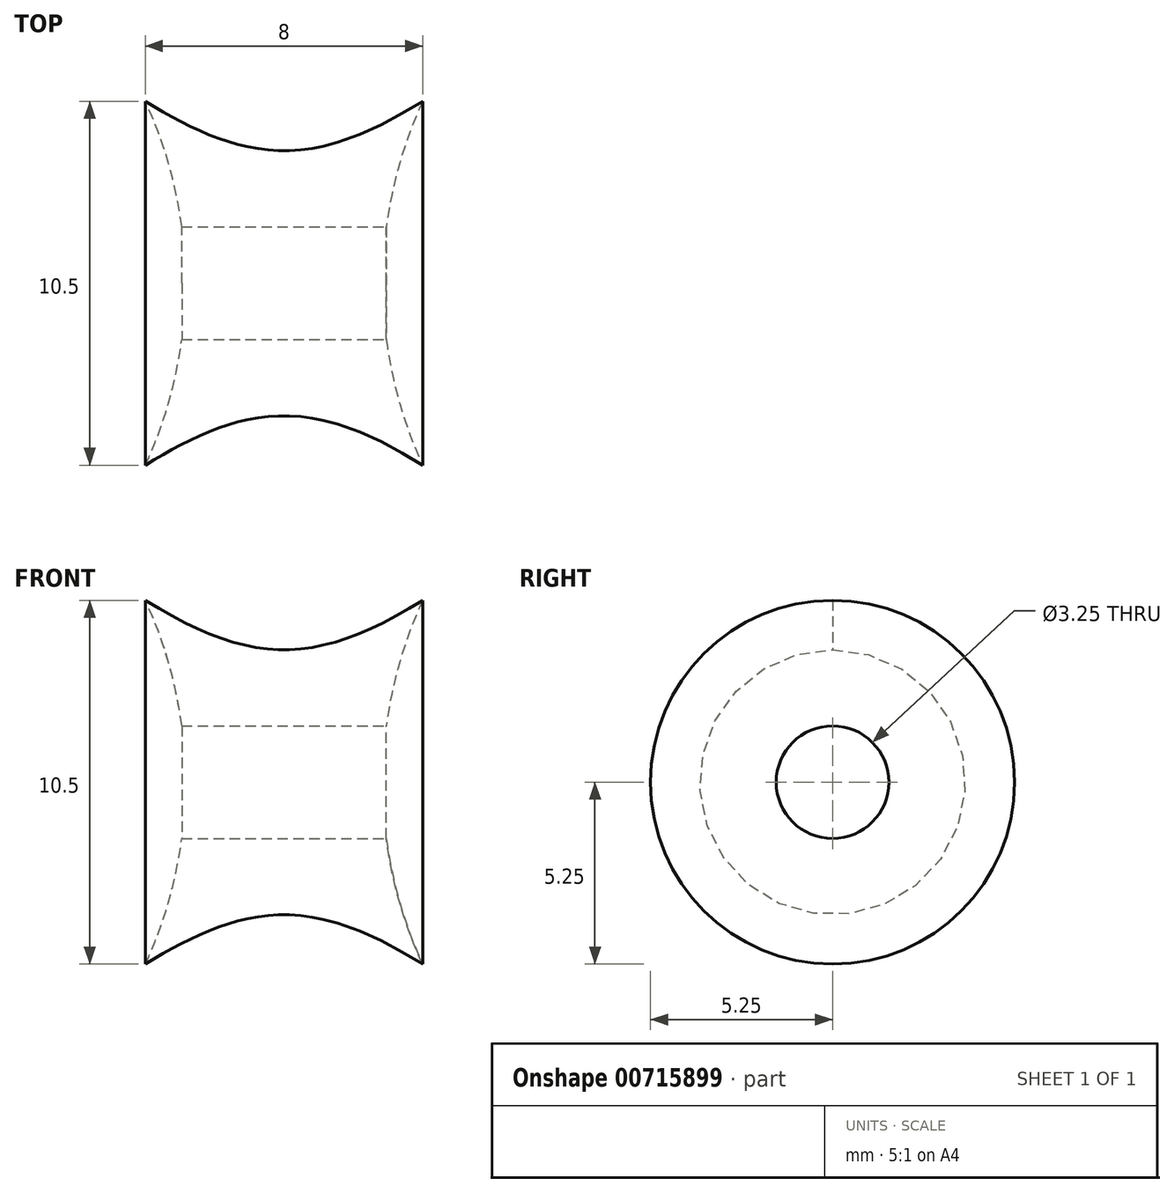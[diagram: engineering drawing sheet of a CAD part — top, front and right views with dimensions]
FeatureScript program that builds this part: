
annotation { "Feature Type Name" : "Feature", "Feature Type Description" : "" }
export const myFeature = defineFeature(function(context is Context, id is Id, definition is map)
    precondition{}
    {
        {
            var Q0;
            Q0=qCreatedBy(makeId("Top.planeOp"),FACE);
            var sketch = newSketch(context, id + "F0", { "sketchPlane" : qUnion([Q0])});
            skArc(sketch, "E0", {"start": v(-28.87, 0) * mm, "mid": v(-16.37, 12.5) * mm, "end": v(-3.87, 0) * mm});
            skLineSegment(sketch, "E1", {"start": v(-28.87, 0) * mm, "end": v(26.82, 0) * mm});
            skArc(sketch, "E2", {"start": v(26.82, 0) * mm, "mid": v(14.32, 12.5) * mm, "end": v(1.82, 0) * mm});
            skFitSpline(sketch, "E3", {"points": [v(-5.03, 5.25) * mm, v(2.97, 5.25) * mm], "startDerivative": vector(9.15, -5.7) * mm, "endDerivative": vector(9.15, 5.7) * mm});
            skSolve(sketch);
        }
        {
            var Q0;
            {var subQ0=sQuery(id+"F0.wireOp",EDGE,"E2");var subQ1=sQuery(id+"F0.wireOp",EDGE,"E1");var subQ2=makeQuery(id+"F0.imprint","INTERSECT",VERTEX,{"disambiguationData":[OD(0.0)],"derivedFrom":[subQ1,subQ0]});Q0=makeQuery(id+"F0.imprint","IMPRINT",FACE,{"disambiguationData":[TD([[makeQuery(id+"F0.imprint","IMPRINT",EDGE,{"disambiguationData":[TD([[subQ2,1.0]])],"derivedFrom":subQ1}),1.0]])]});}
            var Q1;
            {var subQ0=sQuery(id+"F0.wireOp",EDGE,"E1");var subQ1=sQuery(id+"F0.wireOp",EDGE,"E0");var subQ2=makeQuery(id+"F0.imprint","INTERSECT",VERTEX,{"disambiguationData":[OD(0.0)],"derivedFrom":[subQ1,subQ0]});Q1=makeQuery(id+"F0.imprint","IMPRINT",FACE,{"disambiguationData":[TD([[makeQuery(id+"F0.imprint","IMPRINT",EDGE,{"disambiguationData":[TD([[subQ2,-1.0]])],"derivedFrom":subQ1}),-1.0]])]});}
            var Q2;
            {var subQ3=sQuery(id+"F0.wireOp",EDGE,"E3");Q2=makeQuery(id+"F0.imprint","IMPRINT",FACE,{"disambiguationData":[TD([[makeQuery(id+"F0.imprint","IMPRINT",EDGE,{"derivedFrom":subQ3}),-1.0]])]});}
            var Q3;
            Q3=sQuery(id+"F0.wireOp",EDGE,"E1");
            revolve(context, id + "F1", {"entities" : qUnion([Q0, Q1, Q2]), "axis" : qUnion([Q3]), "revolveType" : RevolveType.FULL});
        }
        {
            var Q0;
            Q0=qCreatedBy(makeId("Right.planeOp"),FACE);
            var Q1;
            Q1=sQuery(id+"F0.wireOp",VERTEX,"E2.start");
            cPlane(context, id + "F2", {"entities" : qUnion([Q0, Q1]), "cplaneType" : CPlaneType.PLANE_POINT, "offset" : 25 * mm, "width" : 150 * mm, "height" : 150 * mm});
        }
        {
            var Q0;
            Q0=qCreatedBy(id+"F2.planeOp",FACE);
            var sketch = newSketch(context, id + "F3", { "sketchPlane" : qUnion([Q0])});
            skCircle(sketch, "E4", {"center": v(0, 0) * mm, "radius": 1.62 * mm});
            skSolve(sketch);
        }
        {
            var Q0;
            Q0=qCreatedBy(makeId("Top.planeOp"),FACE);
            cPlane(context, id + "F4", {"entities" : qUnion([Q0]), "cplaneType" : CPlaneType.OFFSET, "offset" : 9.5 * mm, "width" : 150 * mm, "height" : 150 * mm});
        }
        {
            var Q0;
            Q0=qCreatedBy(id+"F4.planeOp",FACE);
            var sketch = newSketch(context, id + "F5", { "sketchPlane" : qUnion([Q0])});
            skCircle(sketch, "E5", {"center": v(15.8, 0) * mm, "radius": 25 * mm});
            skCircle(sketch, "E6", {"center": v(-17.28, 1.86) * mm, "radius": 22.82 * mm});
            skSolve(sketch);
        }
        {
            var Q0;
            Q0=qSketchRegion(id+"F5",true);
            extrude(context, id + "F6", {"entities" : qUnion([Q0]), "operationType" : NewBodyOperationType.REMOVE, "depth" : 25 * mm});
        }
        {
            var Q0;
            Q0=qSketchRegion(id+"F3",true);
            extrude(context, id + "F7", {"entities" : qUnion([Q0]), "operationType" : NewBodyOperationType.REMOVE, "endBound" : BoundingType.THROUGH_ALL, "oppositeDirection" : true, "depth" : 25 * mm});
        }
    });
